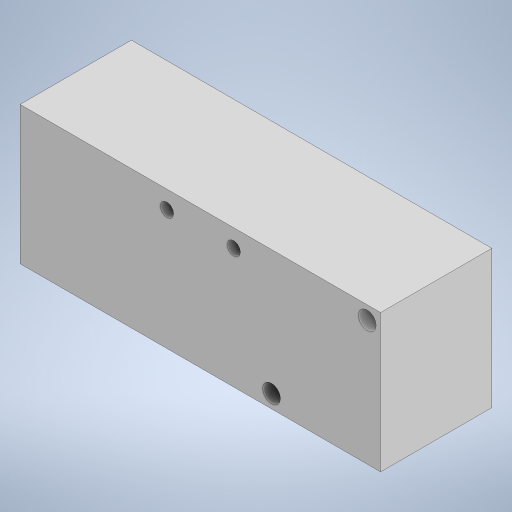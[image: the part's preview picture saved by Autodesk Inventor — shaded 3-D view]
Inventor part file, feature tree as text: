
AUTODESK INVENTOR PART (.ipt)
format: ipt  version: 2023 (Build 270158000, 158)  size: 194,560 bytes
history: native  units: mm
features: extrude x1, sketch x1
ambient origin geometry x8: Origin, YZ Plane, XZ Plane, XY Plane, X Axis, Y Axis, Z Axis, Center Point
bodies: Solid1 (feature_tree)
feature tree (2):
  extrude  "Extrusion1"  Depth=81.0mm
  sketch  "Sketch1"  dims[d0=3.0mm d1=81.0mm d2=31.0mm d3=4.0mm d4=3.0mm d5=24.5mm d6=4.0mm d7=3.0mm d8=30.0mm d9=3.0mm d11=4.0mm d12=15.0mm d13=3.0mm d14=25.0mm d15=0.0mm]
